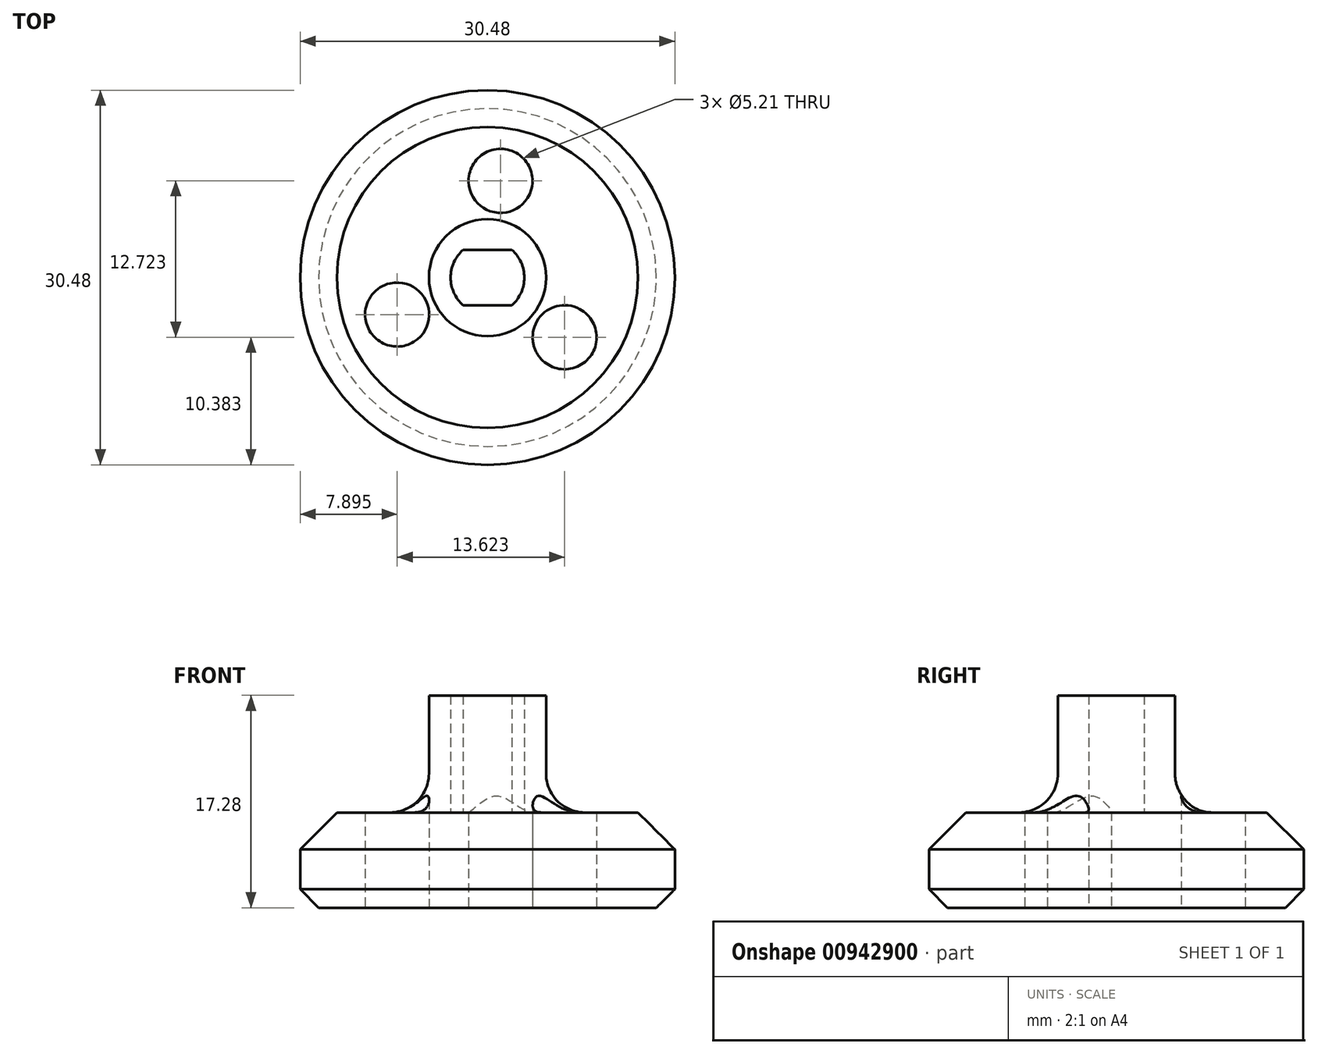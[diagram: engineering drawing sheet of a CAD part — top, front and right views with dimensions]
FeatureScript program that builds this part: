
annotation { "Feature Type Name" : "Feature", "Feature Type Description" : "" }
export const myFeature = defineFeature(function(context is Context, id is Id, definition is map)
    precondition{}
    {
        {
            var Q0;
            Q0=qCreatedBy(makeId("Top.planeOp"),FACE);
            var sketch = newSketch(context, id + "F0", { "sketchPlane" : qUnion([Q0])});
            skCircle(sketch, "E0", {"center": v(0, 0) * mm, "radius": 4.76 * mm});
            skSolve(sketch);
        }
        {
            var Q0;
            Q0=qSketchRegion(id+"F0",true);
            extrude(context, id + "F1", {"entities" : qUnion([Q0]), "depth" : 9.52 * mm, "offsetDistance" : 25.4 * mm, "hasSecondDirection" : true, "secondDirectionOppositeDirection" : true, "secondDirectionDepth" : 6.35 * mm});
        }
        {
            var Q0;
            Q0=qCreatedBy(makeId("Top.planeOp"),FACE);
            var sketch = newSketch(context, id + "F2", { "sketchPlane" : qUnion([Q0])});
            skCircle(sketch, "E1", {"center": v(0, 0) * mm, "radius": 3 * mm});
            skLineSegment(sketch, "E2", {"start": v(-1.98, 2.25) * mm, "end": v(1.98, 2.25) * mm});
            skLineSegment(sketch, "E3", {"start": v(-1.98, -2.25) * mm, "end": v(1.98, -2.25) * mm});
            skSolve(sketch);
        }
        {
            var Q0;
            {var subQ0=sQuery(id+"F2.wireOp",EDGE,"E2");Q0=makeQuery(id+"F2.imprint","IMPRINT",FACE,{"disambiguationData":[TD([[makeQuery(id+"F2.imprint","IMPRINT",EDGE,{"derivedFrom":subQ0}),-1.0]])]});}
            extrude(context, id + "F3", {"entities" : qUnion([Q0]), "operationType" : NewBodyOperationType.REMOVE, "endBound" : BoundingType.THROUGH_ALL, "depth" : 25.4 * mm, "offsetDistance" : 25.4 * mm});
        }
        {
            var Q0;
            Q0=qCreatedBy(makeId("Top.planeOp"),FACE);
            var sketch = newSketch(context, id + "F4", { "sketchPlane" : qUnion([Q0])});
            skCircle(sketch, "E4", {"center": v(0, 0) * mm, "radius": 15.24 * mm});
            skSolve(sketch);
        }
        {
            var Q0;
            Q0=qSketchRegion(id+"F4",true);
            var Q1;
            Q1=sQuery(id+"F4.wireOp",EDGE,"E4");
            extrude(context, id + "F5", {"entities" : qUnion([Q0]), "operationType" : NewBodyOperationType.ADD, "surfaceEntities" : qUnion([Q1]), "oppositeDirection" : true, "depth" : 7.75 * mm, "offsetDistance" : 25.4 * mm});
        }
        {
            var Q0;
            Q0=makeQuery(id+"F5.opExtrude","CAP_FACE",FACE,{"disambiguationData":[OSD([sQuery(id+"F4.wireOp",EDGE,"E4")])],"isStart":false});
            var sketch = newSketch(context, id + "F6", { "sketchPlane" : qUnion([Q0])});
            skCircle(sketch, "E5", {"center": v(6.28, 4.86) * mm, "radius": 2.6 * mm});
            skCircle(sketch, "E6", {"center": v(0, 0) * mm, "radius": 7.94 * mm, "construction": true});
            skCircle(sketch, "E7", {"center": v(-7.35, 3) * mm, "radius": 2.6 * mm});
            skLineSegment(sketch, "E8", {"start": v(6.28, 4.86) * mm, "end": v(-7.35, 3) * mm, "construction": true});
            skLineSegment(sketch, "E9", {"start": v(-7.35, 3) * mm, "end": v(1.07, -7.87) * mm, "construction": true});
            skLineSegment(sketch, "E10", {"start": v(1.07, -7.87) * mm, "end": v(6.28, 4.86) * mm, "construction": true});
            skCircle(sketch, "E11", {"center": v(1.07, -7.87) * mm, "radius": 2.6 * mm});
            skSolve(sketch);
        }
        {
            var Q0;
            Q0=makeQuery(id+"F6.imprint","IMPRINT",FACE,{"disambiguationData":[TD([[makeQuery(id+"F6.imprint","IMPRINT",EDGE,{"derivedFrom":sQuery(id+"F6.wireOp",EDGE,"E11")}),1.0]])]});
            var Q1;
            Q1=makeQuery(id+"F6.imprint","IMPRINT",FACE,{"disambiguationData":[TD([[makeQuery(id+"F6.imprint","IMPRINT",EDGE,{"derivedFrom":sQuery(id+"F6.wireOp",EDGE,"E5")}),1.0]])]});
            var Q2;
            Q2=makeQuery(id+"F6.imprint","IMPRINT",FACE,{"disambiguationData":[TD([[makeQuery(id+"F6.imprint","IMPRINT",EDGE,{"derivedFrom":sQuery(id+"F6.wireOp",EDGE,"E7")}),1.0]])]});
            extrude(context, id + "F7", {"entities" : qUnion([Q0, Q1, Q2]), "operationType" : NewBodyOperationType.REMOVE, "oppositeDirection" : true, "depth" : 13.97 * mm, "offsetDistance" : 25.4 * mm});
        }
        {
            var Q0;
            Q0=makeQuery(id+"F5.opExtrude","CAP_EDGE",EDGE,{"disambiguationData":[OSD([sQuery(id+"F4.wireOp",EDGE,"E4")])],"isStart":false});
            chamfer(context, id + "F8", {"entities" : qUnion([Q0]), "width" : 1.5 * mm, "tangentPropagation" : true});
        }
        {
            var Q0;
            Q0=makeQuery(id+"F5.opExtrude","CAP_EDGE",EDGE,{"disambiguationData":[OSD([sQuery(id+"F4.wireOp",EDGE,"E4")])],"isStart":true});
            chamfer(context, id + "F9", {"entities" : qUnion([Q0]), "width" : 3 * mm, "tangentPropagation" : true});
        }
        {
            var Q0;
            Q0=makeQuery(id+"F5.boolean.opBoolean","INTERSECT",EDGE,{"derivedFrom":[makeQuery(id+"F1.opExtrude","SWEPT_FACE",FACE,{"disambiguationData":[OSD([sQuery(id+"F0.wireOp",EDGE,"E0")])]}),makeQuery(id+"F5.opExtrude","CAP_FACE",FACE,{"disambiguationData":[OSD([sQuery(id+"F4.wireOp",EDGE,"E4")])],"isStart":true})]});
            fillet(context, id + "F10", {"entities" : qUnion([Q0]), "radius" : 3.17 * mm, "tangentPropagation" : true, "allowEdgeOverflow" : false});
        }
    });
